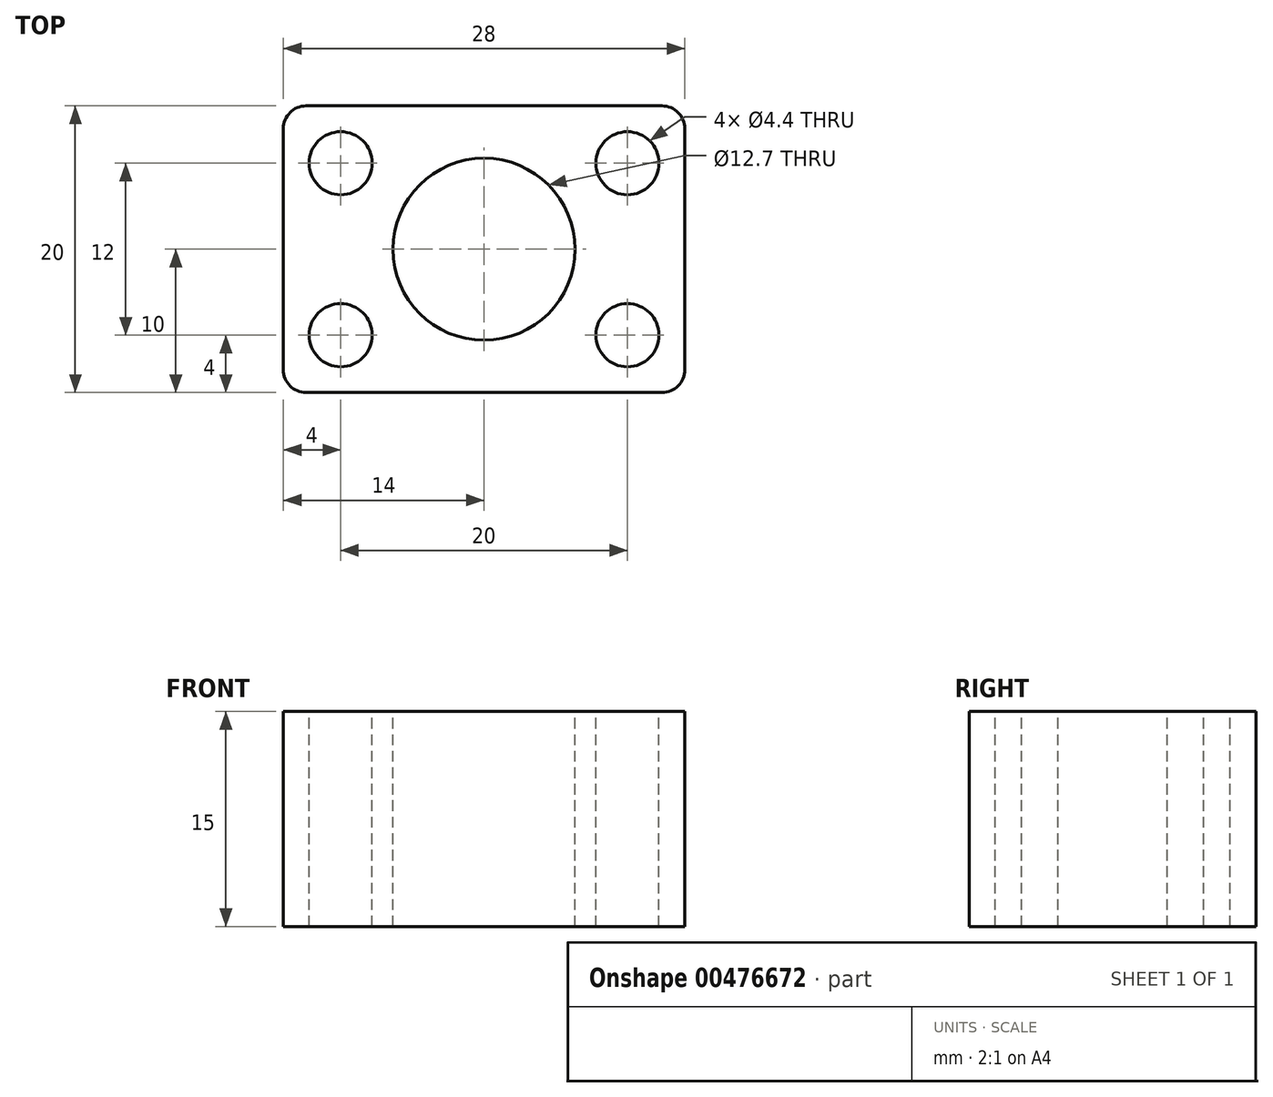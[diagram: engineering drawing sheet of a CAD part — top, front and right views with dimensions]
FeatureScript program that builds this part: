
annotation { "Feature Type Name" : "Feature", "Feature Type Description" : "" }
export const myFeature = defineFeature(function(context is Context, id is Id, definition is map)
    precondition{}
    {
        {
            var Q0;
            Q0=qCreatedBy(makeId("Top.planeOp"),FACE);
            var sketch = newSketch(context, id + "F0", { "sketchPlane" : qUnion([Q0])});
            skLineSegment(sketch, "E0.bottom", {"start": v(0, 0) * mm, "end": v(28, 0) * mm});
            skLineSegment(sketch, "E0.top", {"start": v(0, 20) * mm, "end": v(28, 20) * mm});
            skLineSegment(sketch, "E0.left", {"start": v(0, 0) * mm, "end": v(0, 20) * mm});
            skLineSegment(sketch, "E0.right", {"start": v(28, 0) * mm, "end": v(28, 20) * mm});
            skSolve(sketch);
        }
        {
            var Q0;
            Q0 = qSketchRegion(id + "F0", true);
            extrude(context, id + "F1", {"entities" : qUnion([Q0]), "depth" : 15 * mm});
        }
        {
            var Q0;
            Q0=makeQuery(id+"F1.opExtrude","CAP_FACE",FACE,{"disambiguationData":[OSD([sQuery(id+"F0.wireOp",EDGE,"E0.bottom"),sQuery(id+"F0.wireOp",EDGE,"E0.top"),sQuery(id+"F0.wireOp",EDGE,"E0.left"),sQuery(id+"F0.wireOp",EDGE,"E0.right")])],"isStart":false});
            var sketch = newSketch(context, id + "F2", { "sketchPlane" : qUnion([Q0])});
            skLineSegment(sketch, "E1.bottom", {"start": v(4, 16) * mm, "end": v(24, 16) * mm});
            skLineSegment(sketch, "E1.top", {"start": v(4, 4) * mm, "end": v(24, 4) * mm});
            skLineSegment(sketch, "E1.left", {"start": v(4, 16) * mm, "end": v(4, 4) * mm});
            skLineSegment(sketch, "E1.right", {"start": v(24, 16) * mm, "end": v(24, 4) * mm});
            skLineSegment(sketch, "E2", {"start": v(14, 0) * mm, "end": v(14, 4) * mm, "construction": true});
            skLineSegment(sketch, "E3", {"start": v(14, 16) * mm, "end": v(14, 20) * mm, "construction": true});
            skPoint(sketch, "E4", {"position": v(4, 16) * mm});
            skPoint(sketch, "E5", {"position": v(4, 4) * mm});
            skPoint(sketch, "E6", {"position": v(24, 16) * mm});
            skPoint(sketch, "E7", {"position": v(24, 4) * mm});
            skSolve(sketch);
        }
        {
            var Q0;
            Q0=sQuery(id+"F2.wireOp",VERTEX,"E4");
            var Q1;
            Q1=sQuery(id+"F2.wireOp",VERTEX,"E5");
            var Q2;
            Q2=sQuery(id+"F2.wireOp",VERTEX,"E7");
            var Q3;
            Q3=sQuery(id+"F2.wireOp",VERTEX,"E6");
            var Q4;
            Q4=makeQuery(id+"F1.opExtrude","SWEPT_BODY",BODY,{"disambiguationData":[OSD([sQuery(id+"F0.wireOp",EDGE,"E0.bottom"),sQuery(id+"F0.wireOp",EDGE,"E0.top"),sQuery(id+"F0.wireOp",EDGE,"E0.left"),sQuery(id+"F0.wireOp",EDGE,"E0.right")])]});
            hole(context, id + "F3", {"style" : HoleStyle.SIMPLE, "endStyle" : HoleEndStyle.THROUGH, "standardTappedOrClearance" : lookupTablePath({ "standard" : "ISO", "fit" : "Normal", "size" : "M4", "type" : "Clearance" }), "standardBlindInLast" : lookupTablePath({ "fit" : "Standard", "standard" : "ISO", "size" : "M4", "type" : "Clearance" }), "holeDiameter" : 4.4 * mm, "isTappedThrough" : true, "tappedDepth" : 12.7 * mm, "tapClearance" : 3, "locations" : qUnion([Q0, Q1, Q2, Q3]), "scope" : qUnion([Q4])});
        }
        {
            var Q0;
            Q0=makeQuery(id+"F1.opExtrude","CAP_FACE",FACE,{"disambiguationData":[OSD([sQuery(id+"F0.wireOp",EDGE,"E0.bottom"),sQuery(id+"F0.wireOp",EDGE,"E0.top"),sQuery(id+"F0.wireOp",EDGE,"E0.left"),sQuery(id+"F0.wireOp",EDGE,"E0.right")])],"isStart":false});
            var sketch = newSketch(context, id + "F4", { "sketchPlane" : qUnion([Q0])});
            skCircle(sketch, "E8", {"center": v(14, 10) * mm, "radius": 6.35 * mm});
            skLineSegment(sketch, "E9", {"start": v(0, 10) * mm, "end": v(14, 10) * mm, "construction": true});
            skLineSegment(sketch, "E10", {"start": v(28, 10) * mm, "end": v(14, 10) * mm, "construction": true});
            skSolve(sketch);
        }
        {
            var Q0;
            Q0 = qSketchRegion(id + "F4", true);
            extrude(context, id + "F5", {"entities" : qUnion([Q0]), "operationType" : NewBodyOperationType.REMOVE, "endBound" : BoundingType.THROUGH_ALL, "oppositeDirection" : true, "depth" : 25.4 * mm});
        }
        {
            var Q0;
            Q0=makeQuery(id+"F1.opExtrude","SWEPT_EDGE",EDGE,{"disambiguationData":[OSD([sQuery(id+"F0.wireOp",EDGE,"E0.bottom"),sQuery(id+"F0.wireOp",EDGE,"E0.left")])]});
            var Q1;
            Q1=makeQuery(id+"F1.opExtrude","SWEPT_EDGE",EDGE,{"disambiguationData":[OSD([sQuery(id+"F0.wireOp",EDGE,"E0.bottom"),sQuery(id+"F0.wireOp",EDGE,"E0.right")])]});
            var Q2;
            Q2=makeQuery(id+"F1.opExtrude","SWEPT_EDGE",EDGE,{"disambiguationData":[OSD([sQuery(id+"F0.wireOp",EDGE,"E0.top"),sQuery(id+"F0.wireOp",EDGE,"E0.right")])]});
            var Q3;
            Q3=makeQuery(id+"F1.opExtrude","SWEPT_EDGE",EDGE,{"disambiguationData":[OSD([sQuery(id+"F0.wireOp",EDGE,"E0.top"),sQuery(id+"F0.wireOp",EDGE,"E0.left")])]});
            fillet(context, id + "F6", {"entities" : qUnion([Q0, Q1, Q2, Q3]), "radius" : 1.59 * mm, "tangentPropagation" : true, "allowEdgeOverflow" : false});
        }
    });
